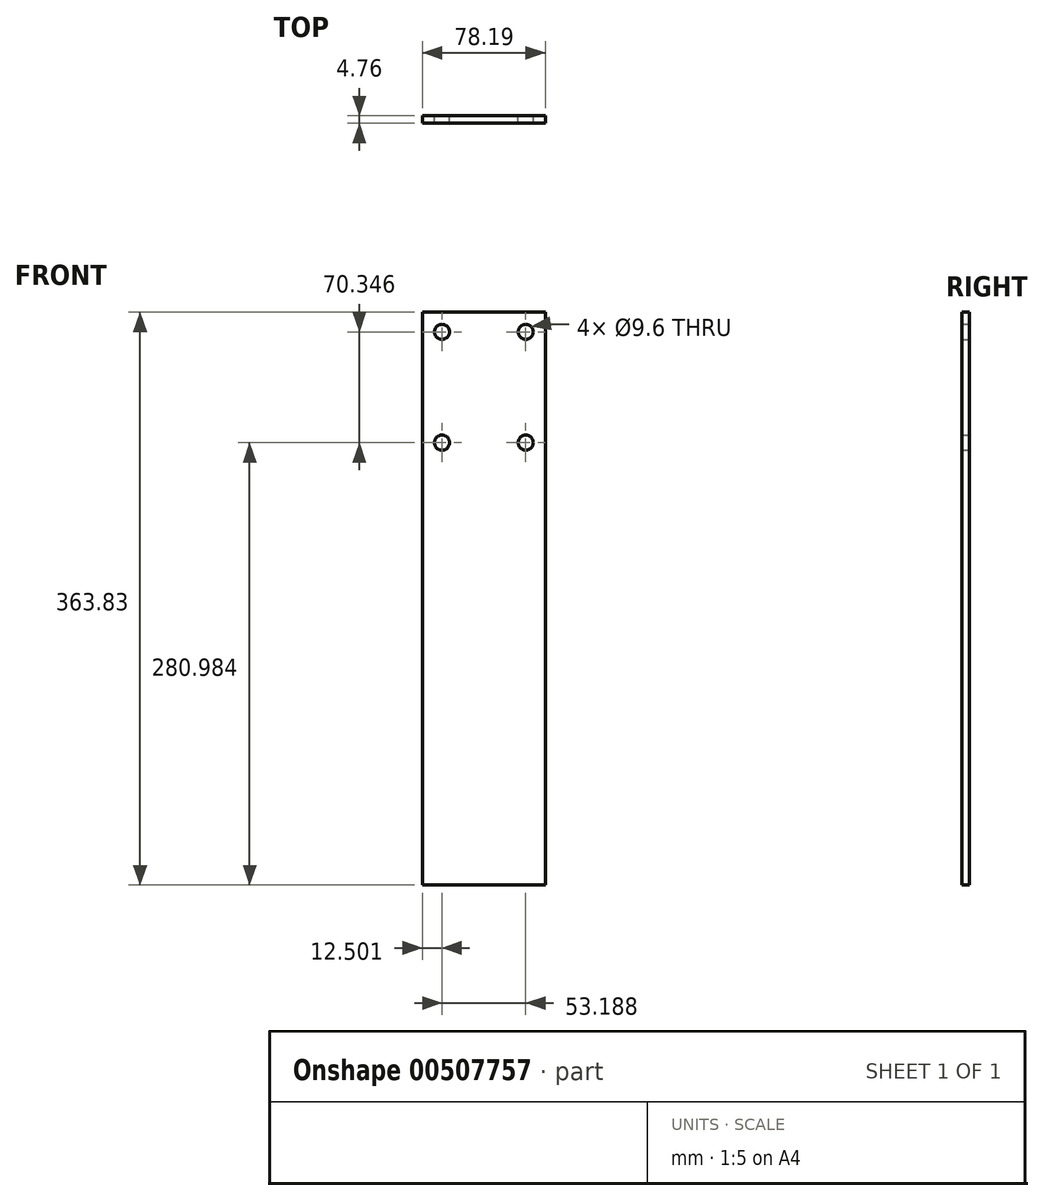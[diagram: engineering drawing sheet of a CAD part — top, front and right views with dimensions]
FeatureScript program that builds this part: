
annotation { "Feature Type Name" : "Feature", "Feature Type Description" : "" }
export const myFeature = defineFeature(function(context is Context, id is Id, definition is map)
    precondition{}
    {
        {
            var Q0;
            Q0=qCreatedBy(makeId("Front.planeOp"),FACE);
            var sketch = newSketch(context, id + "F0", { "sketchPlane" : qUnion([Q0])});
            skLineSegment(sketch, "E0.bottom", {"start": v(30.1, 53.48) * mm, "end": v(-48.08, 53.48) * mm});
            skLineSegment(sketch, "E0.top", {"start": v(30.1, -310.35) * mm, "end": v(-48.08, -310.35) * mm});
            skLineSegment(sketch, "E0.left", {"start": v(30.1, 53.48) * mm, "end": v(30.1, -310.35) * mm});
            skLineSegment(sketch, "E0.right", {"start": v(-48.08, 53.48) * mm, "end": v(-48.08, -310.35) * mm});
            skSolve(sketch);
        }
        {
            var Q0;
            Q0=qCreatedBy(makeId("Front.planeOp"),FACE);
            var sketch = newSketch(context, id + "F1", { "sketchPlane" : qUnion([Q0])});
            skCircle(sketch, "E1", {"center": v(-35.58, 40.98) * mm, "radius": 4.8 * mm});
            skCircle(sketch, "E2", {"center": v(17.6, 40.98) * mm, "radius": 4.8 * mm});
            skCircle(sketch, "E3", {"center": v(17.6, -29.37) * mm, "radius": 4.8 * mm});
            skCircle(sketch, "E4", {"center": v(-35.58, -29.37) * mm, "radius": 4.8 * mm});
            skSolve(sketch);
        }
        {
            var Q0;
            Q0=makeQuery(id+"F0.imprint","IMPRINT",FACE,{"disambiguationData":[TD([[makeQuery(id+"F0.imprint","IMPRINT",EDGE,{"derivedFrom":sQuery(id+"F0.wireOp",EDGE,"E0.bottom")}),1.0]])]});
            extrude(context, id + "F2", {"entities" : qUnion([Q0]), "depth" : 4.76 * mm});
        }
        {
            var Q0;
            Q0 = qSketchRegion(id + "F1", true);
            extrude(context, id + "F3", {"entities" : qUnion([Q0]), "operationType" : NewBodyOperationType.REMOVE, "endBound" : BoundingType.THROUGH_ALL, "depth" : 25 * mm});
        }
    });
